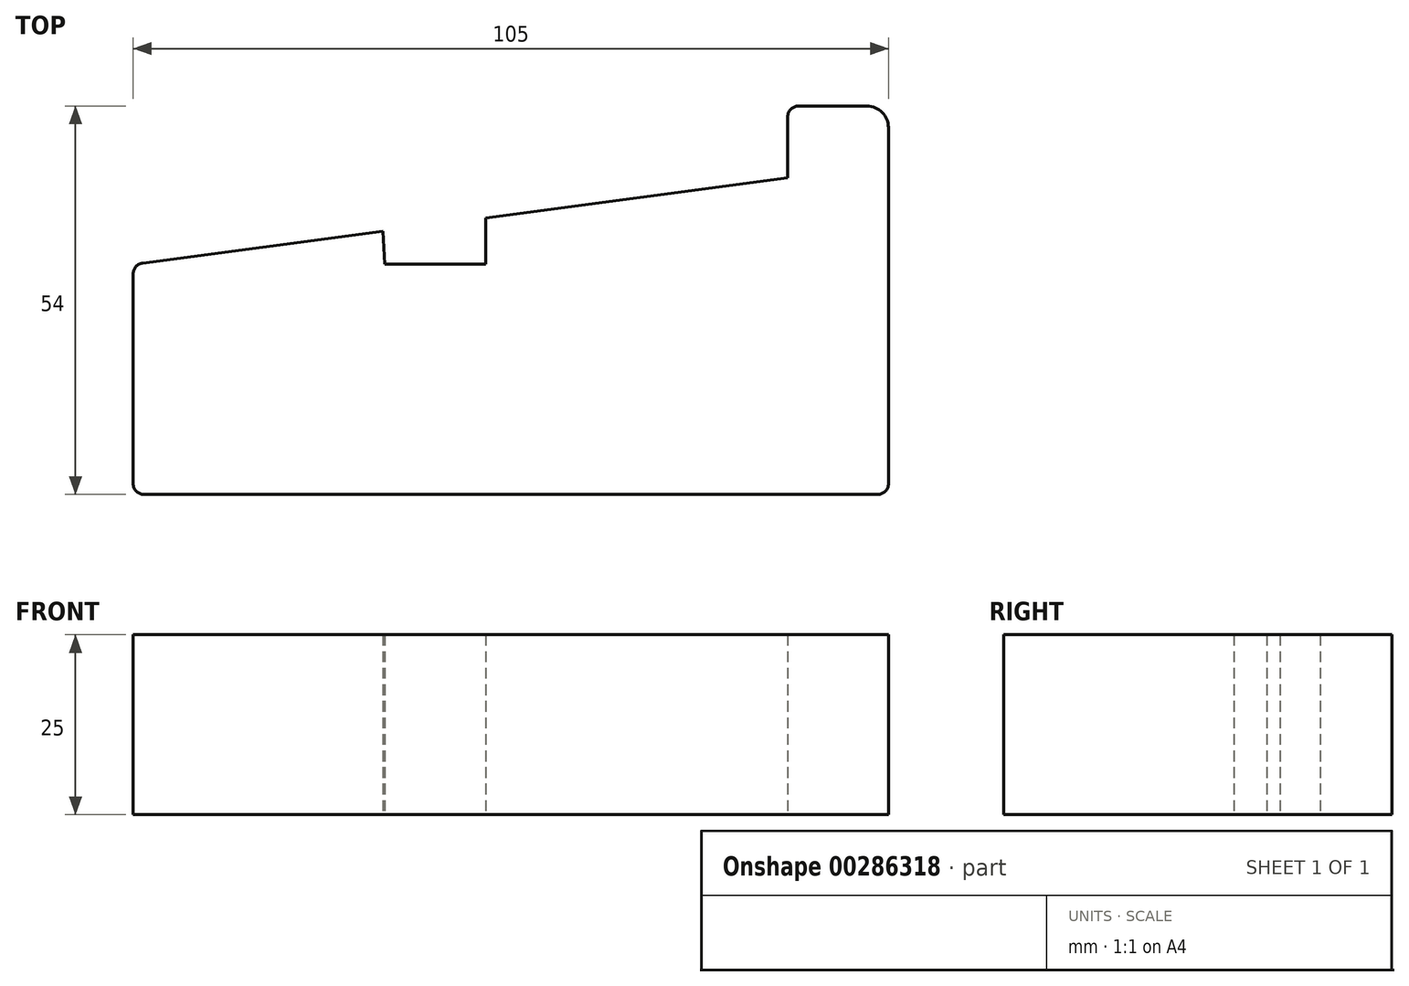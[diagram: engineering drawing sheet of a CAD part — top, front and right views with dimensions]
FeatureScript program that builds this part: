
annotation { "Feature Type Name" : "Feature", "Feature Type Description" : "" }
export const myFeature = defineFeature(function(context is Context, id is Id, definition is map)
    precondition{}
    {
        {
            var Q0;
            Q0=qCreatedBy(makeId("Top.planeOp"),FACE);
            var sketch = newSketch(context, id + "F0", { "sketchPlane" : qUnion([Q0])});
            skLineSegment(sketch, "E0", {"start": v(-57.73, -42.22) * mm, "end": v(45.77, -42.22) * mm});
            skLineSegment(sketch, "E1", {"start": v(47.27, -40.72) * mm, "end": v(47.27, 8.78) * mm});
            skLineSegment(sketch, "E2", {"start": v(44.27, 11.78) * mm, "end": v(34.77, 11.78) * mm});
            skLineSegment(sketch, "E3", {"start": v(33.27, 10.28) * mm, "end": v(33.27, 1.78) * mm});
            skLineSegment(sketch, "E4", {"start": v(-57.73, -40.72) * mm, "end": v(-57.73, -11.53) * mm});
            skLineSegment(sketch, "E5", {"start": v(-8.73, -42.22) * mm, "end": v(-57.73, -42.22) * mm});
            skPoint(sketch, "E6.start.orphan", {"position": v(-22.73, -14.38) * mm});
            skPoint(sketch, "E7.start.orphan", {"position": v(-8.73, -10.22) * mm});
            skLineSegment(sketch, "E8", {"start": v(-56.23, -42.22) * mm, "end": v(-22.73, -42.22) * mm});
            skLineSegment(sketch, "E9", {"start": v(-22.73, -42.22) * mm, "end": v(-8.73, -42.22) * mm});
            skLineSegment(sketch, "E10", {"start": v(-57.73, -10.22) * mm, "end": v(-23.03, -5.64) * mm});
            skLineSegment(sketch, "E11", {"start": v(-56.43, -10.05) * mm, "end": v(-23.03, -5.64) * mm});
            skLineSegment(sketch, "E12", {"start": v(-8.73, -3.76) * mm, "end": v(33.27, 1.78) * mm});
            skLineSegment(sketch, "E13", {"start": v(-23.03, -5.64) * mm, "end": v(-22.73, -10.22) * mm});
            skLineSegment(sketch, "E14", {"start": v(-22.73, -10.22) * mm, "end": v(-8.73, -10.22) * mm});
            skLineSegment(sketch, "E15", {"start": v(-8.73, -3.76) * mm, "end": v(-8.73, -10.22) * mm});
            skPoint(sketch, "E16.visualSharp", {"position": v(-57.73, -42.22) * mm});
            skArc(sketch, "E16.filletArc", {"start": v(-57.73, -40.72) * mm, "mid": v(-57.3, -41.78) * mm, "end": v(-56.23, -42.22) * mm});
            skPoint(sketch, "E17.visualSharp", {"position": v(-57.73, -10.22) * mm});
            skArc(sketch, "E17.filletArc", {"start": v(-56.43, -10.05) * mm, "mid": v(-57.36, -10.54) * mm, "end": v(-57.73, -11.53) * mm});
            skPoint(sketch, "E18.visualSharp", {"position": v(47.27, -42.22) * mm});
            skArc(sketch, "E18.filletArc", {"start": v(45.77, -42.22) * mm, "mid": v(46.83, -41.78) * mm, "end": v(47.27, -40.72) * mm});
            skPoint(sketch, "E19.visualSharp", {"position": v(33.27, 11.78) * mm});
            skArc(sketch, "E19.filletArc", {"start": v(34.77, 11.78) * mm, "mid": v(33.7, 11.34) * mm, "end": v(33.27, 10.28) * mm});
            skPoint(sketch, "E20.visualSharp", {"position": v(47.27, 11.78) * mm});
            skArc(sketch, "E20.filletArc", {"start": v(47.27, 8.78) * mm, "mid": v(46.39, 10.9) * mm, "end": v(44.27, 11.78) * mm});
            skSolve(sketch);
        }
        {
            var Q0;
            Q0 = qSketchRegion(id + "F0", true);
            extrude(context, id + "F1", {"entities" : qUnion([Q0]), "depth" : 25 * mm});
        }
    });
